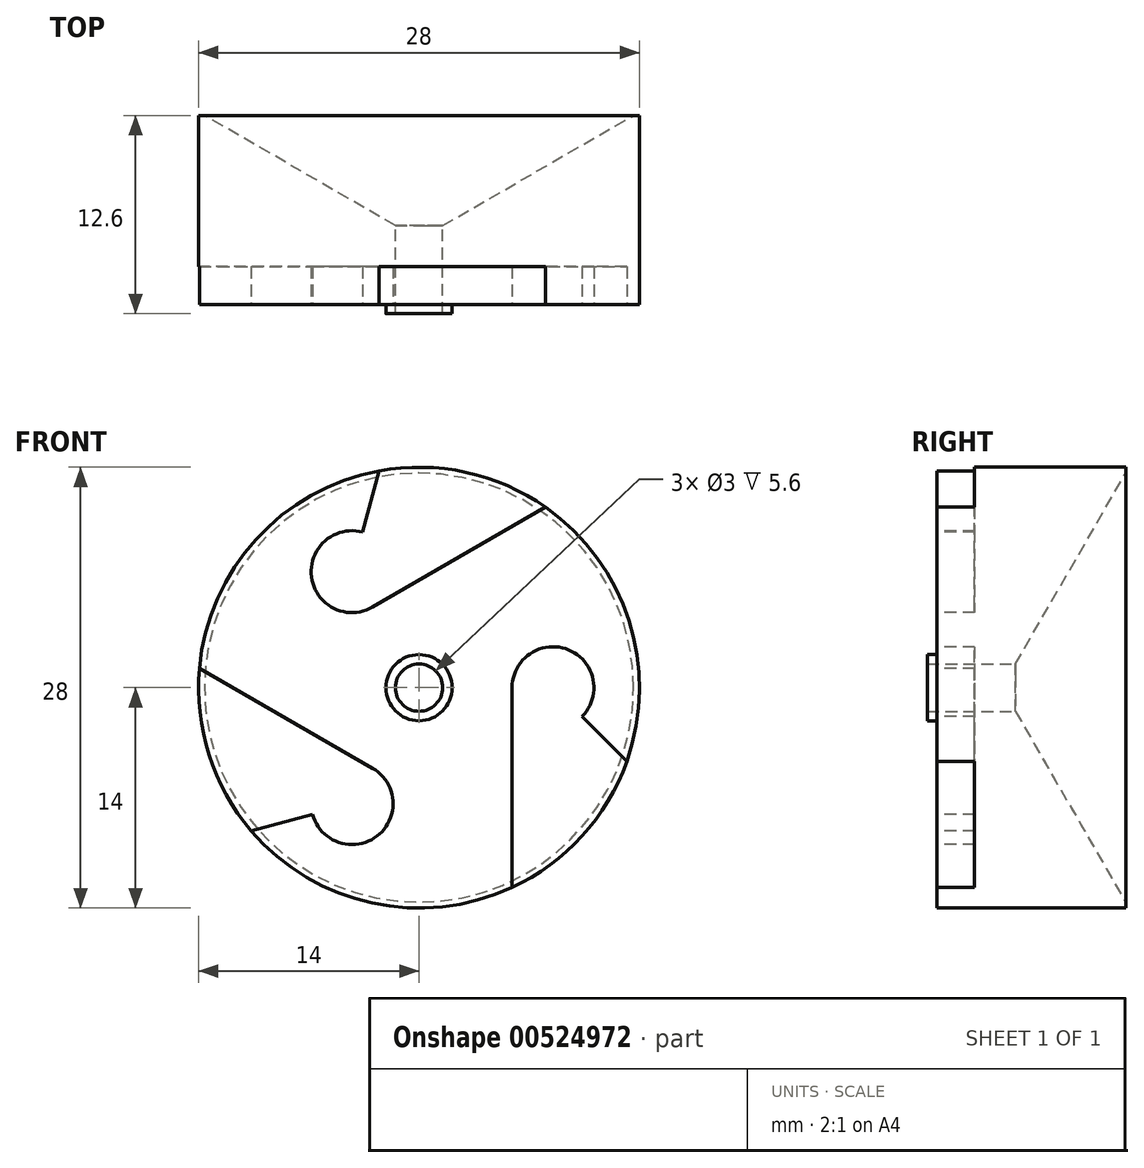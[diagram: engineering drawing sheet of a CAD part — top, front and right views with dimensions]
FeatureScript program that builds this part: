
annotation { "Feature Type Name" : "Feature", "Feature Type Description" : "" }
export const myFeature = defineFeature(function(context is Context, id is Id, definition is map)
    precondition{}
    {
        {
            var Q0;
            Q0=qCreatedBy(makeId("Front.planeOp"),FACE);
            var sketch = newSketch(context, id + "F0", { "sketchPlane" : qUnion([Q0])});
            skCircle(sketch, "E0", {"center": v(0, 0) * mm, "radius": 14 * mm});
            skCircle(sketch, "E1", {"center": v(0, 0) * mm, "radius": 1.5 * mm});
            skSolve(sketch);
        }
        {
            var Q0;
            Q0=makeQuery(id+"F0.imprint","IMPRINT",FACE,{"disambiguationData":[TD([[makeQuery(id+"F0.imprint","IMPRINT",EDGE,{"derivedFrom":sQuery(id+"F0.wireOp",EDGE,"E0")}),1.0]])]});
            var Q1;
            Q1=makeQuery(id+"F0.imprint","IMPRINT",FACE,{"disambiguationData":[TD([[makeQuery(id+"F0.imprint","IMPRINT",EDGE,{"derivedFrom":sQuery(id+"F0.wireOp",EDGE,"E1")}),-1.0]])]});
            extrude(context, id + "F1", {"entities" : qUnion([Q0, Q1]), "depth" : 12 * mm, "offsetDistance" : 25 * mm});
        }
        {
            var Q0;
            Q0=makeQuery(id+"F1.opExtrude","CAP_EDGE",EDGE,{"disambiguationData":[OSD([sQuery(id+"F0.wireOp",EDGE,"E1")])],"isStart":true});
            chamfer(context, id + "F2", {"entities" : qUnion([Q0]), "chamferType" : ChamferType.OFFSET_ANGLE, "width" : 7 * mm, "oppositeDirection" : true, "angle" : 60 * degree, "tangentPropagation" : true});
        }
        {
            var Q0;
            Q0=makeQuery(id+"F1.opExtrude","CAP_FACE",FACE,{"disambiguationData":[OSD([sQuery(id+"F0.wireOp",EDGE,"E0"),sQuery(id+"F0.wireOp",EDGE,"E1")])],"isStart":false});
            var sketch = newSketch(context, id + "F3", { "sketchPlane" : qUnion([Q0])});
            skLineSegment(sketch, "E2", {"start": v(17.01, 0) * mm, "end": v(0, 0) * mm, "construction": true});
            skLineSegment(sketch, "E3", {"start": v(-8.5, 14.74) * mm, "end": v(0, 0) * mm, "construction": true});
            skLineSegment(sketch, "E4", {"start": v(0, 0) * mm, "end": v(-8.5, -14.74) * mm, "construction": true});
            skCircle(sketch, "E5", {"center": v(0, 0) * mm, "radius": 8.5 * mm, "construction": true});
            skCircle(sketch, "E6", {"center": v(-4.25, -7.37) * mm, "radius": 2.6 * mm});
            skArc(sketch, "E7", {"start": v(10.35, -1.84) * mm, "mid": v(9.5, 2.4) * mm, "end": v(5.9, 0) * mm});
            skCircle(sketch, "E8", {"center": v(-4.25, 7.37) * mm, "radius": 2.6 * mm});
            skLineSegment(sketch, "E9", {"start": v(5.9, 0) * mm, "end": v(5.9, -12.7) * mm});
            skArc(sketch, "E10", {"start": v(5.9, -12.7) * mm, "mid": v(10.36, -9.42) * mm, "end": v(13.2, -4.69) * mm});
            skLineSegment(sketch, "E11", {"start": v(13.2, -4.69) * mm, "end": v(10.35, -1.84) * mm});
            skCircle(sketch, "E12", {"center": v(0, 0) * mm, "radius": 2.1 * mm});
            skSolve(sketch);
        }
        {
            var Q0;
            {var subQ0=sQuery(id+"F3.wireOp",EDGE,"E7");Q0=makeQuery(id+"F3.imprint","IMPRINT",FACE,{"disambiguationData":[TD([[makeQuery(id+"F3.imprint","IMPRINT",EDGE,{"derivedFrom":subQ0}),1.0]])]});}
            extrude(context, id + "F4", {"entities" : qUnion([Q0]), "operationType" : NewBodyOperationType.ADD, "depth" : 1 * mm, "offsetDistance" : 25 * mm});
        }
        {
            var Q0;
            Q0=makeQuery(id+"F3.imprint","IMPRINT",FACE,{"disambiguationData":[TD([[makeQuery(id+"F3.imprint","IMPRINT",EDGE,{"derivedFrom":sQuery(id+"F3.wireOp",EDGE,"E12")}),1.0]])]});
            extrude(context, id + "F5", {"entities" : qUnion([Q0]), "operationType" : NewBodyOperationType.ADD, "depth" : 0.6 * mm, "offsetDistance" : 25 * mm});
        }
        {
            var Q0;
            Q0=makeQuery(id+"F1.opExtrude","SWEPT_BODY",BODY,{"disambiguationData":[OSD([sQuery(id+"F0.wireOp",EDGE,"E0"),sQuery(id+"F0.wireOp",EDGE,"E1")])]});
            var Q1;
            Q1=sQuery(id+"F3.wireOp",EDGE,"E5");
            circularPattern(context, id + "F6", {"entities" : qUnion([Q0]), "axis" : qUnion([Q1]), "angle" : 360 * degree, "instanceCount" : 3, "equalSpace" : true, "computeTransformsWithoutBuiltin" : true});
        }
        {
            var Q0;
            Q0=makeQuery(id+"F4.opExtrude","CAP_FACE",FACE,{"disambiguationData":[OSD([sQuery(id+"F0.wireOp",EDGE,"E0"),sQuery(id+"F3.wireOp",EDGE,"E7"),sQuery(id+"F3.wireOp",EDGE,"E9"),sQuery(id+"F3.wireOp",EDGE,"E11")])],"isStart":false});
            var Q1;
            Q1=makeQuery(id+"F6.opPattern","COPY",FACE,{"derivedFrom":makeQuery(id+"F4.opExtrude","CAP_FACE",FACE,{"disambiguationData":[OSD([sQuery(id+"F0.wireOp",EDGE,"E0"),sQuery(id+"F3.wireOp",EDGE,"E7"),sQuery(id+"F3.wireOp",EDGE,"E9"),sQuery(id+"F3.wireOp",EDGE,"E11")])],"isStart":false}),"instanceName":"2"});
            var Q2;
            Q2=makeQuery(id+"F6.opPattern","COPY",FACE,{"derivedFrom":makeQuery(id+"F4.opExtrude","CAP_FACE",FACE,{"disambiguationData":[OSD([sQuery(id+"F0.wireOp",EDGE,"E0"),sQuery(id+"F3.wireOp",EDGE,"E7"),sQuery(id+"F3.wireOp",EDGE,"E9"),sQuery(id+"F3.wireOp",EDGE,"E11")])],"isStart":false}),"instanceName":"1"});
            extrude(context, id + "F7", {"entities" : qUnion([Q0, Q1, Q2]), "operationType" : NewBodyOperationType.REMOVE, "oppositeDirection" : true, "depth" : 3.4 * mm, "offsetDistance" : 25 * mm});
        }
    });
